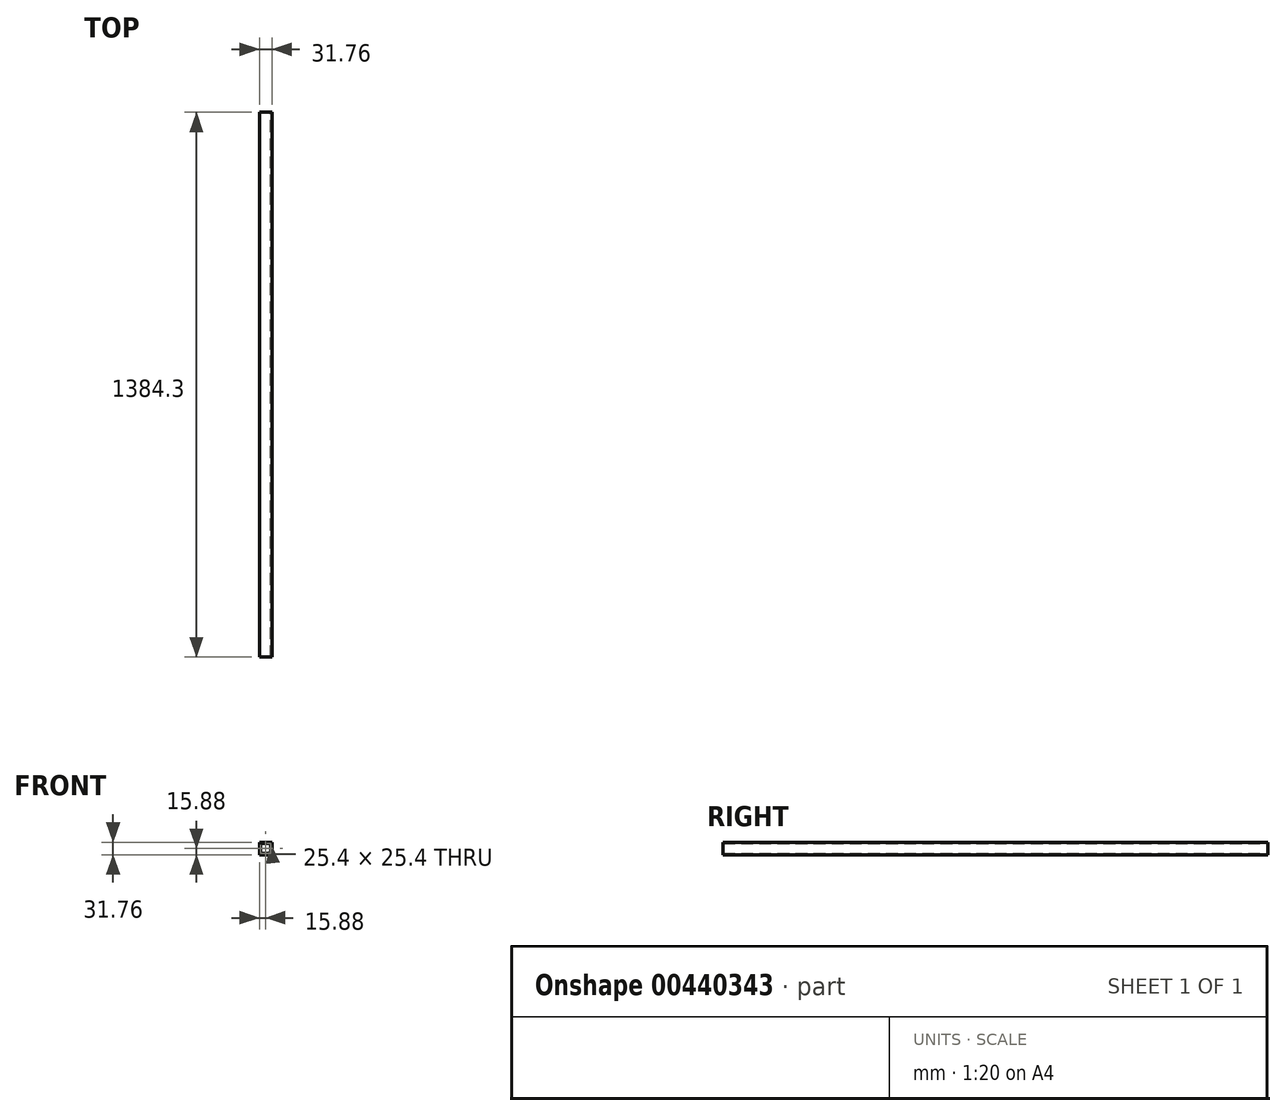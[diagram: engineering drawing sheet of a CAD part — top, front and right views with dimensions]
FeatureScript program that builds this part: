
annotation { "Feature Type Name" : "Feature", "Feature Type Description" : "" }
export const myFeature = defineFeature(function(context is Context, id is Id, definition is map)
    precondition{}
    {
        {
            var Q0;
            Q0=qCreatedBy(makeId("Front.planeOp"),FACE);
            var sketch = newSketch(context, id + "F0", { "sketchPlane" : qUnion([Q0])});
            skLineSegment(sketch, "E0.bottom", {"start": v(-15.87, 15.87) * mm, "end": v(15.88, 15.87) * mm});
            skLineSegment(sketch, "E0.top", {"start": v(-15.88, -15.88) * mm, "end": v(15.87, -15.88) * mm});
            skLineSegment(sketch, "E0.left", {"start": v(-15.87, 15.87) * mm, "end": v(-15.88, -15.88) * mm});
            skLineSegment(sketch, "E0.right", {"start": v(15.88, 15.87) * mm, "end": v(15.87, -15.88) * mm});
            skPoint(sketch, "E0.middle", {"position": v(0, 0) * mm});
            skLineSegment(sketch, "E1.bottom", {"start": v(-12.7, 12.7) * mm, "end": v(12.7, 12.7) * mm});
            skLineSegment(sketch, "E1.top", {"start": v(-12.7, -12.7) * mm, "end": v(12.7, -12.7) * mm});
            skLineSegment(sketch, "E1.left", {"start": v(-12.7, 12.7) * mm, "end": v(-12.7, -12.7) * mm});
            skLineSegment(sketch, "E1.right", {"start": v(12.7, 12.7) * mm, "end": v(12.7, -12.7) * mm});
            skSolve(sketch);
        }
        {
            var Q0;
            Q0=makeQuery(id+"F0.imprint","IMPRINT",FACE,{"disambiguationData":[TD([[makeQuery(id+"F0.imprint","IMPRINT",EDGE,{"derivedFrom":sQuery(id+"F0.wireOp",EDGE,"E0.bottom")}),-1.0]])]});
            extrude(context, id + "F1", {"entities" : qUnion([Q0]), "endBound" : BoundingType.SYMMETRIC, "depth" : 1384.3 * mm});
        }
    });
